# Revit family: Showerhead-DXV-Equility-D3510977X_Series
name_source: partatom
category: Plumbing Fixtures
revit_build: Autodesk Revit 2014 (Build: 20130308_1515(x64)
units: mm (PartAtom-declared; Revit-internal decimal feet)

## types (6) — shared parameters
Assembly Code = D2010710
CW Connection = No
CWFU = 3
CalGreen Compliant = Yes
Default Elevation = 79 5/32"
Description = Equility Multifunction Showerhead
HW Connection = No
HWFU = 3
Height = 6 11/32"
Installation Type = Wall Mounted
Length = 9 3/4"
Manufacturer = DXV
Price = Prices may vary. Please consult Manufacturer Representative for most up-to-date price list.
Product Documentation Link = https://dxv01.blob.core.windows.net
Product Page URL = https://www.dxv.com
Revised Date = 1/14/2019
Tempered Water Connection = Yes
Tempered Water Connection Diameter = 1/2"
Tempered Water Connection Radius = 1/4"
URL = http://www.dxv.com
Vent Connection = No
WFU = 4
Warranty Documentation Link = https://www.dxv.com
Waste Connection = No
Width = 5 7/8"

## per-type parameters (varying)
| type | Finish | Flow Rate | Material |
| D35109775.100 | Metal-DXV-100-Polished Chrome | 2.0 GPM (7.6L/min) | Metal-DXV-100-Polished Chrome |
| D35109775.144 | Metal-DXV-144-Brushed Nickel | 2.0 GPM (7.6L/min) | Metal-DXV-144-Brushed Nickel |
| D35109775.243 | Metal-DXV-243-Matte Black | 2.0 GPM (7.6L/min) | Metal-DXV-243-Matte Black |
| D3510977C.100 | Metal-DXV-100-Polished Chrome | 1.8 GPM (6.8L/min) | Metal-DXV-100-Polished Chrome |
| D3510977C.144 | Metal-DXV-144-Brushed Nickel | 1.8 GPM (6.8L/min) | Metal-DXV-144-Brushed Nickel |
| D3510977C.243 | Metal-DXV-243-Matte Black | 1.8 GPM (6.8L/min) | Metal-DXV-243-Matte Black |

note: column(s) folded — value = type name in every type: Model

## geometry (parser evidence)
native form markers: Sweep x3
no freeform markers — native parametric forms only
